# Revit family: TCAT14-CM
name_source: partatom
category: Lighting Fixtures
units: mm (PartAtom-declared; Revit-internal decimal feet)

## family parameters
Cut with Voids When Loaded = No
Host = Face
Light Source = No
OmniClass Number = 23.80.70.11
OmniClass Title = Luminaries for Internal Lighting
Part Type = Normal
Room Calculation Point = No
Round Connector Dimension = Use Diameter
Shared = No

## types (1)
- TCAT14
    Apparent Load = 0 VA
    Backbox = White
    Certifications = UL1598, 2108 & CSA
    Default Elevation = 48 "
    Description = 1'x 4'LED Twin Contempory Architectural Troffer.
    Lamp = LED Lamp
    Light Bulb = White Glass
    Load Classification = Lighting
    Manufacturer = Columbia Lighting
    Model = TCAT14
    Photometric Web = Web TCAT14 : TCAT14-30MLx-EDU
    Row Length = 48 "
    Suspension Height = 24 "
    URL = https://www.currentlighting.com
    Voltage = 120 V
    Warranty = Five year warranty
    Wattage Comments = 21-58 W
    Watts = 58 W
    Width = 12 "
    zz Length = 47 "

## geometry (parser evidence)
native form markers: Sweep x6
no freeform markers — native parametric forms only
